# Revit family: Flr_Drn_2142_JRSmith
name_source: partatom
category: Plumbing Fixtures
units: mm (PartAtom-declared; Revit-internal decimal feet)

## family parameters
Always vertical = Yes
Cut with Voids When Loaded = No
Part Type = Normal
Room Calculation Point = No
Round Connector Dimension = Use Radius
Shared = No
Work Plane-Based = Yes

## types (5) — shared parameters
04 CSI = 22 13 19
95 CSI = 15155
Assembly Code = D2030300
B = 5"
Caulk Connection = Yes
Default Elevation = 0"
Description = Duco cast iron body and flashing collar with cast iron grate and slotted sediment bucket
Free Area (Sq.In) = 25.5
Manufacturer = Jay R. Smith Mfg. Co.
Material = Cast Iron
Material Finish = Duco Cast Iron
Model = 2230
No-Hub Connection = Yes
OmniClass Code = 22-22 13 19 13
OmniClass Title = Sanitary Drains
Product URL = http://www.jrsmith.com
Push On Connection = Yes
SMARTBIM Object Version = 3
SMARTBIM URL = www.smartbim.com
Technical and Installation = http://www.jrsmith.com
Threaded Connection = Yes
URL = http://www.jrsmith.com
Vent Connection = No
Warranty = 1 year material and workmanship
Waste Connection = No

## per-type parameters (varying)
| type | Outlet Diameter | Outlet Radius | Weight (lb) |
| 2142-02 | 2" | 1" | 48.97 |
| 2142-03 | 3" | 1 1/2" | 47.97 |
| 2142-04 | 4" | 2" | 46.31 |
| 2142-05 | 5" | 2 1/2" | 48.92 |
| 2142-06 | 6" | 3" | 47.08 |

## geometry (parser evidence)
native form markers: Sweep x7
no freeform markers — native parametric forms only
